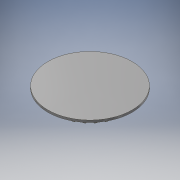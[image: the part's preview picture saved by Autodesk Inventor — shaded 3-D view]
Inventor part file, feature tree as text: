
AUTODESK INVENTOR PART (.ipt)
format: ipt  version: 2017 (Build 210142000, 142)  size: 291,328 bytes
history: native  units: mm (DEFAULTED — no unit token found)
features: sketch x5, extrude x4, plane x3, other x3
ambient origin geometry x8: Origin, YZ Plane, XZ Plane, XY Plane, X Axis, Y Axis, Z Axis, Center Point
bodies: Solid1 (feature_tree)
feature tree (15):
  extrude  "Extrusion1"  Depth=5.0mm TaperAngle=0.0deg
  plane  "Work Plane2"
  plane  "Work Plane8"
  plane  "Work Plane9"
  other  "Spur Gear"
  extrude  "Extrusion2"  Depth=10.0mm TaperAngle=0.0deg
  extrude  "Extrusion3"  Depth=1.121997mm TaperAngle=0.0deg
  extrude  "Extrusion4"  TaperAngle=0.0deg  [1 undecoded]
  sketch  "Sketch1"  dims[d0=67.5mm d1=5.0mm d2=0.0mm]
  sketch  "Sketch2"  dims[d3=63.0mm d4=10.0mm d5=0.0mm]
  other  "Srf1"
  sketch  "Sketch3"  dims[d16=63.0mm d17=0.0mm d34=1.121997mm]
  sketch  "Sketch4"  dims[d39=0.0mm d41=0.0mm]
  sketch  "Sketch5"  dims[d43=63.0mm d46=63.0mm d47=0.0mm d48=0.0mm d49=8.0mm d50=10.0mm d51=0.0mm d52=20.0mm d53=20.0mm d54=3.4mm d55=10.0mm d56=0.0mm d57=80.0mm d58=2.0mm d59=0.0mm]
  other  "Pitch Diameter"
note: 1 required parameter value undecoded (feature->parameter linkage not recoverable at this tier; creation-order binding heuristic only, values carry confidence <= 0.55)
